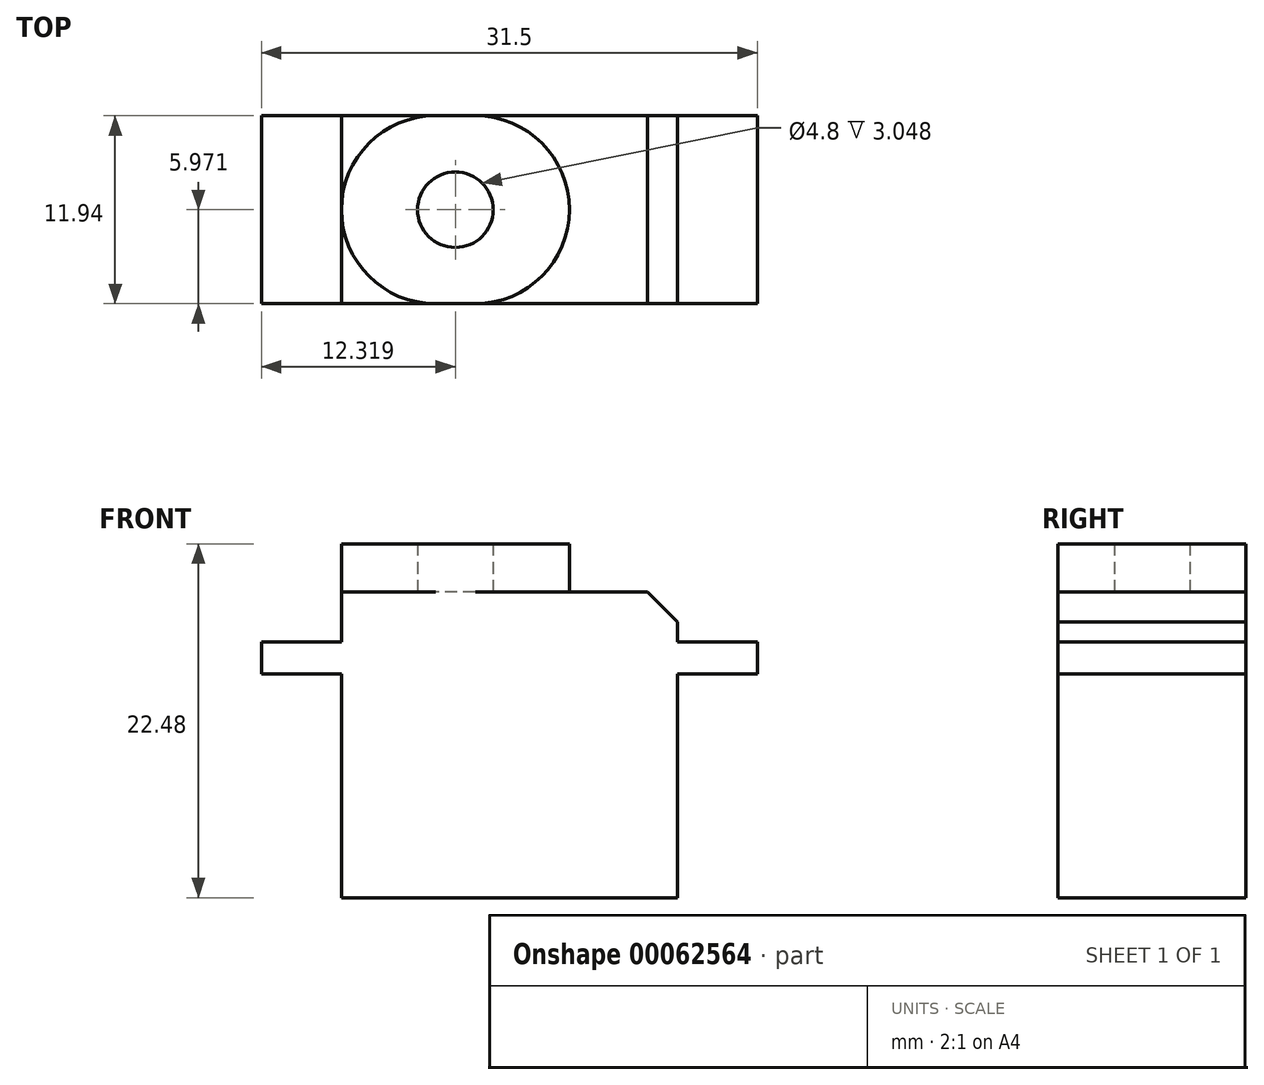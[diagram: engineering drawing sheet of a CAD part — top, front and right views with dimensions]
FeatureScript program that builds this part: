
annotation { "Feature Type Name" : "Feature", "Feature Type Description" : "" }
export const myFeature = defineFeature(function(context is Context, id is Id, definition is map)
    precondition{}
    {
        {
            var Q0;
            Q0=qCreatedBy(makeId("Front.planeOp"),FACE);
            var sketch = newSketch(context, id + "F0", { "sketchPlane" : qUnion([Q0])});
            skLineSegment(sketch, "E0.bottom", {"start": v(0, 0) * mm, "end": v(21.34, 0) * mm});
            skLineSegment(sketch, "E0.top", {"start": v(0, -19.43) * mm, "end": v(21.34, -19.43) * mm});
            skLineSegment(sketch, "E0.left", {"start": v(0, 0) * mm, "end": v(0, -19.43) * mm});
            skLineSegment(sketch, "E0.right", {"start": v(21.34, 0) * mm, "end": v(21.34, -19.43) * mm});
            skLineSegment(sketch, "E1.bottom", {"start": v(0, -3.18) * mm, "end": v(-5.08, -3.18) * mm});
            skLineSegment(sketch, "E1.top", {"start": v(0, -5.2) * mm, "end": v(-5.08, -5.2) * mm});
            skLineSegment(sketch, "E1.left", {"start": v(0, -3.18) * mm, "end": v(0, -5.2) * mm});
            skLineSegment(sketch, "E1.right", {"start": v(-5.08, -3.18) * mm, "end": v(-5.08, -5.2) * mm});
            skLineSegment(sketch, "E2.bottom", {"start": v(0, 0) * mm, "end": v(14.48, 0) * mm});
            skLineSegment(sketch, "E2.top", {"start": v(0, 3.17) * mm, "end": v(14.48, 3.17) * mm});
            skLineSegment(sketch, "E2.left", {"start": v(0, 0) * mm, "end": v(0, 3.17) * mm});
            skLineSegment(sketch, "E2.right", {"start": v(14.48, 0) * mm, "end": v(14.48, 3.17) * mm});
            skLineSegment(sketch, "E3.bottom", {"start": v(26.42, -3.17) * mm, "end": v(21.34, -3.17) * mm});
            skLineSegment(sketch, "E3.top", {"start": v(26.42, -5.2) * mm, "end": v(21.34, -5.2) * mm});
            skLineSegment(sketch, "E3.left", {"start": v(26.42, -3.17) * mm, "end": v(26.42, -5.2) * mm});
            skLineSegment(sketch, "E3.right", {"start": v(21.34, -3.17) * mm, "end": v(21.34, -5.2) * mm});
            skSolve(sketch);
        }
        {
            var Q0;
            Q0=makeQuery(id+"F0.imprint","IMPRINT",FACE,{"disambiguationData":[TD([[makeQuery(id+"F0.imprint","IMPRINT",EDGE,{"derivedFrom":sQuery(id+"F0.wireOp",EDGE,"E1.bottom")}),1.0]])]});
            var Q1;
            Q1=makeQuery(id+"F0.imprint","IMPRINT",FACE,{"disambiguationData":[TD([[makeQuery(id+"F0.imprint","IMPRINT",EDGE,{"derivedFrom":sQuery(id+"F0.wireOp",EDGE,"E3.bottom")}),1.0]])]});
            var Q2;
            {var subQ4=sQuery(id+"F0.wireOp",EDGE,"E0.bottom");Q2=makeQuery(id+"F0.imprint","IMPRINT",FACE,{"disambiguationData":[TD([[makeQuery(id+"F0.imprint","IMPRINT",EDGE,{"derivedFrom":subQ4}),-1.0]])]});}
            extrude(context, id + "F1", {"entities" : qUnion([Q0, Q1, Q2]), "depth" : 11.94 * mm});
        }
        {
            var Q0;
            Q0=makeQuery(id+"F1.opExtrude","SWEPT_EDGE",EDGE,{"disambiguationData":[OSD([sQuery(id+"F0.wireOp",EDGE,"E0.bottom"),sQuery(id+"F0.wireOp",EDGE,"E0.right")])]});
            chamfer(context, id + "F2", {"entities" : qUnion([Q0]), "width" : 1.9 * mm, "tangentPropagation" : true});
        }
        {
            var Q0;
            Q0=makeQuery(id+"F1.opExtrude","SWEPT_FACE",FACE,{"disambiguationData":[OSD([sQuery(id+"F0.wireOp",EDGE,"E0.bottom"),sQuery(id+"F0.wireOp",EDGE,"E2.bottom")])]});
            var sketch = newSketch(context, id + "F3", { "sketchPlane" : qUnion([Q0])});
            skLineSegment(sketch, "E4", {"start": v(0, -5.97) * mm, "end": v(19.43, -5.97) * mm, "construction": true});
            skCircle(sketch, "E5", {"center": v(0, -5.97) * mm, "radius": 5.97 * mm, "construction": true});
            skCircle(sketch, "E6", {"center": v(5.97, -5.97) * mm, "radius": 5.97 * mm});
            skCircle(sketch, "E7", {"center": v(8.5, -5.97) * mm, "radius": 5.97 * mm});
            skLineSegment(sketch, "E8", {"start": v(5.97, 0) * mm, "end": v(8.5, 0) * mm});
            skLineSegment(sketch, "E9", {"start": v(5.97, -11.94) * mm, "end": v(8.5, -11.94) * mm});
            skLineSegment(sketch, "E10", {"start": v(5.97, -5.97) * mm, "end": v(7.24, -5.97) * mm});
            skLineSegment(sketch, "E11", {"start": v(7.24, -5.97) * mm, "end": v(8.5, -5.97) * mm});
            skCircle(sketch, "E12", {"center": v(7.24, -5.97) * mm, "radius": 2.4 * mm});
            skSolve(sketch);
        }
        {
            var Q0;
            Q0 = qSketchRegion(id + "F3", true);
            var Q1;
            {var subQ0=sQuery(id+"F3.wireOp",EDGE,"E7");var subQ1=sQuery(id+"F3.wireOp",EDGE,"E6");var subQ2=makeQuery(id+"F3.imprint","INTERSECT",VERTEX,{"disambiguationData":[OD(0.0)],"derivedFrom":[subQ1,subQ0]});Q1=makeQuery(id+"F3.imprint","IMPRINT",FACE,{"disambiguationData":[TD([[makeQuery(id+"F3.imprint","IMPRINT",EDGE,{"disambiguationData":[TD([[subQ2,1.0]])],"derivedFrom":subQ1}),1.0]])]});}
            extrude(context, id + "F4", {"entities" : qUnion([Q0, Q1]), "operationType" : NewBodyOperationType.ADD, "depth" : 3.05 * mm});
        }
    });
